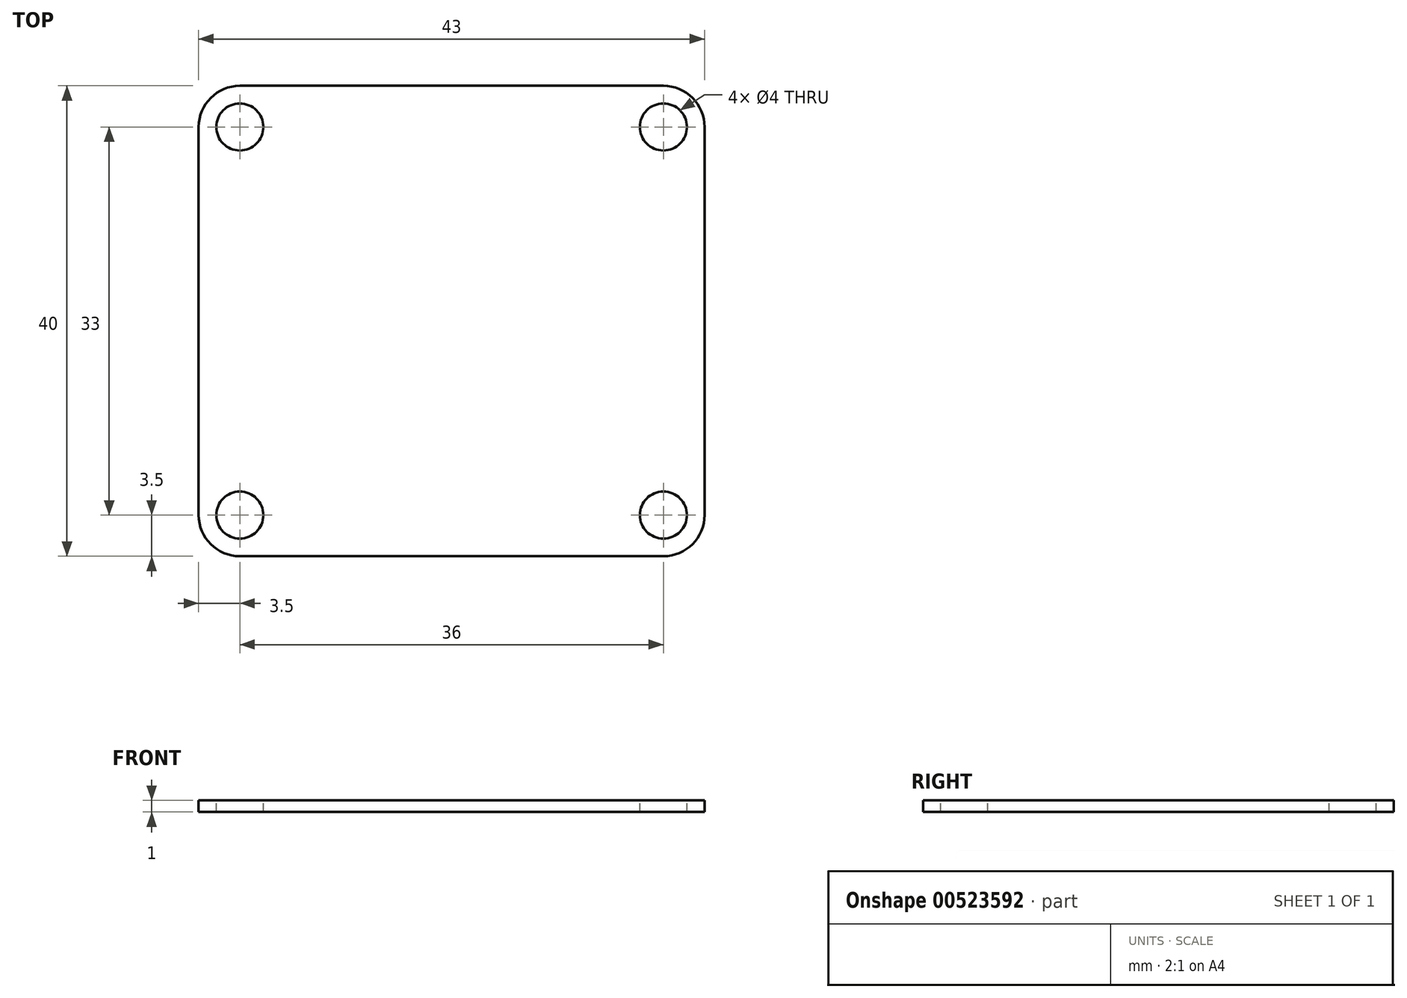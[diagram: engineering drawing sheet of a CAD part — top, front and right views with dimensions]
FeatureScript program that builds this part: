
annotation { "Feature Type Name" : "Feature", "Feature Type Description" : "" }
export const myFeature = defineFeature(function(context is Context, id is Id, definition is map)
    precondition{}
    {
        {
            var Q0;
            Q0=qCreatedBy(makeId("Top.planeOp"),FACE);
            var sketch = newSketch(context, id + "F0", { "sketchPlane" : qUnion([Q0])});
            skLineSegment(sketch, "E0.bottom", {"start": v(18, -20) * mm, "end": v(-18, -20) * mm});
            skLineSegment(sketch, "E0.top", {"start": v(18, 20) * mm, "end": v(-18, 20) * mm});
            skLineSegment(sketch, "E0.left", {"start": v(21.5, -16.5) * mm, "end": v(21.5, 16.5) * mm});
            skLineSegment(sketch, "E0.right", {"start": v(-21.5, -16.5) * mm, "end": v(-21.5, 16.5) * mm});
            skPoint(sketch, "E0.middle", {"position": v(0, 0) * mm});
            skPoint(sketch, "E1.visualSharp", {"position": v(-21.5, 20) * mm});
            skArc(sketch, "E1.filletArc", {"start": v(-18, 20) * mm, "mid": v(-20.47, 18.97) * mm, "end": v(-21.5, 16.5) * mm});
            skPoint(sketch, "E2.visualSharp", {"position": v(21.5, 20) * mm});
            skArc(sketch, "E2.filletArc", {"start": v(21.5, 16.5) * mm, "mid": v(20.47, 18.97) * mm, "end": v(18, 20) * mm});
            skPoint(sketch, "E3.visualSharp", {"position": v(21.5, -20) * mm});
            skArc(sketch, "E3.filletArc", {"start": v(18, -20) * mm, "mid": v(20.47, -18.97) * mm, "end": v(21.5, -16.5) * mm});
            skPoint(sketch, "E4.visualSharp", {"position": v(-21.5, -20) * mm});
            skArc(sketch, "E4.filletArc", {"start": v(-21.5, -16.5) * mm, "mid": v(-20.47, -18.97) * mm, "end": v(-18, -20) * mm});
            skLineSegment(sketch, "E5.bottom", {"start": v(18, -16.5) * mm, "end": v(-18, -16.5) * mm, "construction": true});
            skLineSegment(sketch, "E5.top", {"start": v(18, 16.5) * mm, "end": v(-18, 16.5) * mm, "construction": true});
            skLineSegment(sketch, "E5.left", {"start": v(18, -16.5) * mm, "end": v(18, 16.5) * mm, "construction": true});
            skLineSegment(sketch, "E5.right", {"start": v(-18, -16.5) * mm, "end": v(-18, 16.5) * mm, "construction": true});
            skCircle(sketch, "E6", {"center": v(-18, 16.5) * mm, "radius": 2 * mm});
            skCircle(sketch, "E7", {"center": v(18, 16.5) * mm, "radius": 2 * mm});
            skCircle(sketch, "E8", {"center": v(18, -16.5) * mm, "radius": 2 * mm});
            skCircle(sketch, "E9", {"center": v(-18, -16.5) * mm, "radius": 2 * mm});
            skSolve(sketch);
        }
        {
            var Q0;
            Q0=makeQuery(id+"F0.imprint","IMPRINT",FACE,{"disambiguationData":[TD([[makeQuery(id+"F0.imprint","IMPRINT",EDGE,{"derivedFrom":sQuery(id+"F0.wireOp",EDGE,"E0.bottom")}),-1.0]])]});
            extrude(context, id + "F1", {"entities" : qUnion([Q0]), "oppositeDirection" : true, "depth" : 1 * mm, "offsetDistance" : 25 * mm});
        }
    });
